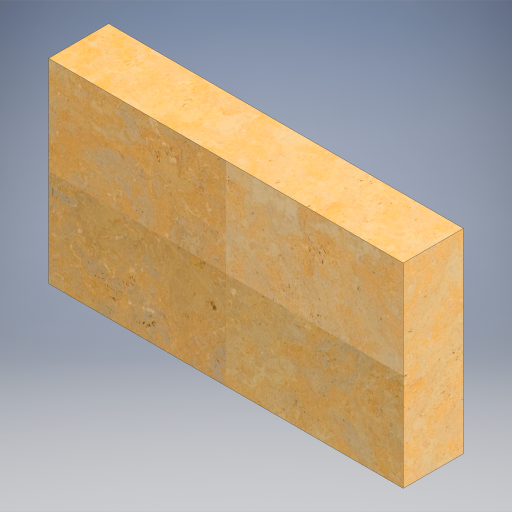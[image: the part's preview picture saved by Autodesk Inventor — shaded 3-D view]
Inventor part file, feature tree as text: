
AUTODESK INVENTOR PART (.ipt)
format: ipt  version: 2023 (Build 270158030, 158C)  size: 512,000 bytes
history: native  units: in
note: dims shown in document units (in); Inventor stores cm internally (conversion verified against a paired STEP export)
features: extrude x1, sketch x1
ambient origin geometry x8: Origin, YZ Plane, XZ Plane, XY Plane, X Axis, Y Axis, Z Axis, Center Point
bodies: Solid1 (feature_tree)
feature tree (2):
  extrude  "Extrusion1"  Depth=13.0in
  sketch  "Sketch1"  dims[d0=23.625in d1=13.0in d2=4.0in d3=0.0in]
